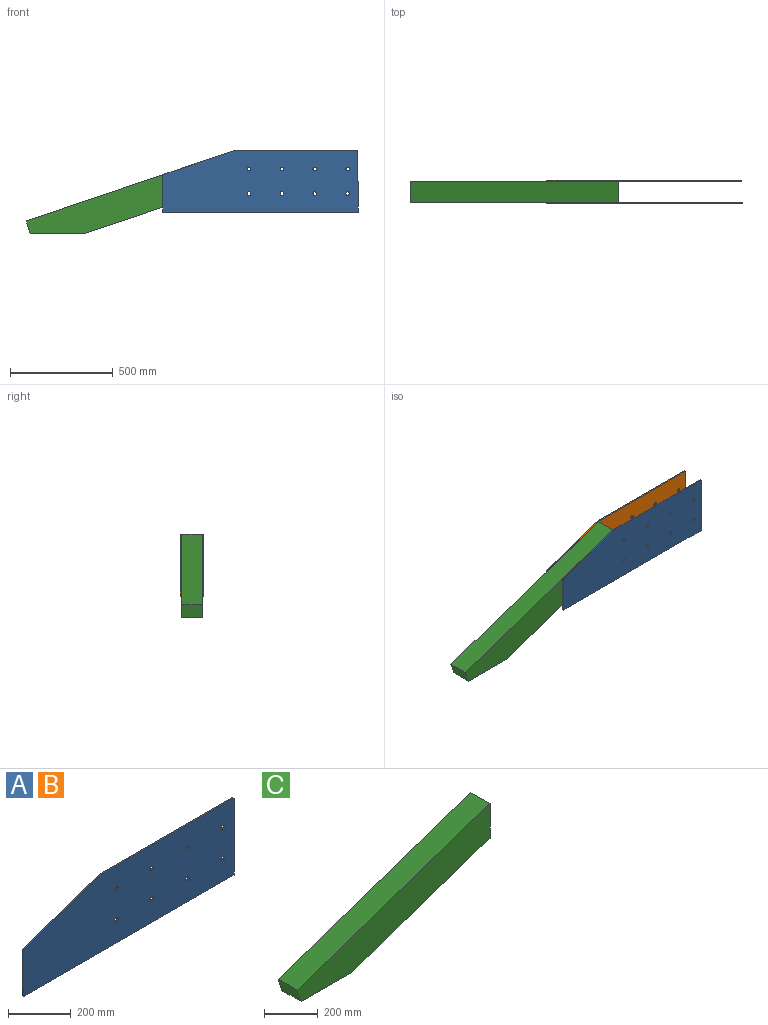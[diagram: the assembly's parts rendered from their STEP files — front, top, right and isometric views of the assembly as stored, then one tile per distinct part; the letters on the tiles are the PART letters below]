
ASSEMBLY  parts=3 mates=6
PART A: 15 faces, bbox 948.6x6x300 mm
  f0: plane 182.16x6mm, normal (-1,0,0), area 1092.9mm2, adj f1,f4,f5,f6
  f1: plane 948.65x6mm, normal (0,0,-1), area 5691.9mm2, adj f0,f2,f5,f6
  f2: plane 300x6mm, normal (1,0,0), area 1800mm2, adj f1,f3,f5,f6
  f3: plane 600x6mm, normal (0,0,1), area 3600mm2, adj f2,f4,f5,f6
  f4: plane 348.65x117.84mm, normal (-0.32,0,0.95), area 2208.1mm2, adj f0,f3,f5,f6
  f5: plane 948.65x300mm, normal (0,1,0), area 262015.3mm2, adj f0,f1,f2,f3,f4,f7,f8,f9
  f6: plane 948.65x300mm, normal (0,-1,0), area 262015.3mm2, adj f0,f1,f2,f3,f4,f7,f8,f9
  f7: cylinder r=9mm len=18mm, axis (0,-1,0), area 339.3mm2, adj f5,f6
  f8: cylinder r=9mm len=18mm, axis (0,-1,0), area 339.3mm2, adj f5,f6
  f9: cylinder r=9mm len=18mm, axis (0,-1,0), area 339.3mm2, adj f5,f6
  f10: cylinder r=9mm len=18mm, axis (0,-1,0), area 339.3mm2, adj f5,f6
  f11: cylinder r=9mm len=18mm, axis (0,-1,0), area 339.3mm2, adj f5,f6
  f12: cylinder r=9mm len=18mm, axis (0,-1,0), area 339.3mm2, adj f5,f6
  f13: cylinder r=9mm len=18mm, axis (0,-1,0), area 339.3mm2, adj f5,f6
  f14: cylinder r=9mm len=18mm, axis (0,-1,0), area 339.3mm2, adj f5,f6
PART B: same geometry as A
PART C: 7 faces, bbox 1014.6x100x405 mm
  f0: plane 158.34x100mm, normal (1,0,0), area 15833.7mm2, adj f1,f4,f5,f6
  f1: plane 1014.57x342.93mm, normal (-0.32,0,0.95), area 107095.3mm2, adj f0,f2,f5,f6
  f2: plane 100x62.07mm, normal (-0.95,0,-0.32), area 6552.5mm2, adj f1,f3,f5,f6
  f3: plane 263.82x100mm, normal (0,0,-1), area 26381.6mm2, adj f2,f4,f5,f6
  f4: plane 729.77x246.66mm, normal (0.32,0,-0.95), area 77032.7mm2, adj f0,f3,f5,f6
  f5: plane 1014.57x405mm, normal (0,-1,0), area 146284.2mm2, adj f0,f1,f2,f3,f4
  f6: plane 1014.57x405mm, normal (0,1,0), area 146284.2mm2, adj f0,f1,f2,f3,f4
PLACE A t=(-781.45,262.94,67.7)mm
PLACE B t=(-781.45,368.94,67.7)mm
PLACE C t=(-781.45,368.94,67.7)mm
MATE planar B.f4 <-> C.f1  axis (-0.32,0,0.95) through (2.87,371.94,423.78)mm
MATE revolute C.f6 <-> B.f6  axis (0,1,0) through (177.2,368.94,482.7)mm
MATE planar B.f2 <-> A.f2  axis (1,0,0) through (777.2,371.94,332.7)mm
MATE planar B.f6 <-> C.f6  axis (0,-1,0) through (329.52,368.94,324.02)mm
MATE planar A.f4 <-> C.f1  axis (-0.32,0,0.95) through (2.87,265.94,423.78)mm
MATE planar A.f5 <-> C.f5  axis (0,1,0) through (329.52,268.94,324.02)mm
